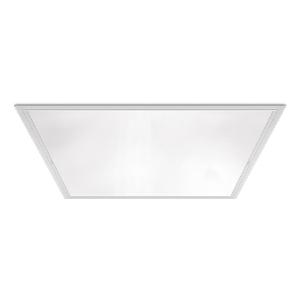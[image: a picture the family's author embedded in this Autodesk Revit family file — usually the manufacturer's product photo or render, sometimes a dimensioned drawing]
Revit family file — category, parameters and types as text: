
# Revit family: 3f_filippi_-_l_340_luce_diffusa_lgs_ip65v_3f_filippi_-_23977_-_l_340_45w-840_lgs_ip65v_621x621
name_source: partatom
category: Lighting Fixtures
units: mm (PartAtom-declared; Revit-internal decimal feet)

## family parameters
Cut with Voids When Loaded = No
Host = Face
Light Source = No
Part Type = Normal
Room Calculation Point = No
Round Connector Dimension = Use Diameter
Shared = No

## types (1)
- 3F Filippi - L 340 Luce Diffusa LGS IP65V (1 x LED, 6537 lm, 52 W, 4000 K)
    Apparent Load = 52 VA
    Approval mark = ENEC
    CIE Flux Codes = 67 92 98 100 100
    Color Rendering = 80
    Color Temperature = 4000 K
    Control Gear = Electronic ballast
    Default Elevation = 1800 mm
    Description = ILLUMINOTECHNICAL
Luminous efficiency 100% (DLOR 100%, ULOR 0%).
Initial luminous flux of the luminaire 6537 lm.
Direct symmetric distribution.
Installation Interdistance Transv.D = 1.19 x hu - Long.D = 1.17 x hu.
Average luminance <3000 cd/m² for radial angles >65°.
Tabular UGR (CIE 117 - 4H-8H; S=0.25H; 70/50/20): RUG 18.3 - 18.3.
Beam angle: 87° - 86°.
Luminous efficacy 126 lm/W.
Lifetime (L93/B10): 30000 h. (tq+25°C)
Lifetime (L90/B10): 50000 h. (tq+25°C)
Lifetime (L85/B10): 80000 h. (tq+25°C)
Lifetime (L80/B10): 100000 h. (tq+25°C)
Sudden decreased luminous flux after 50000 hours: 0% (C0).
Photobiological safety in compliance with IEC/TR 62778: RG0 risk exempt, (IEC 62471).
In compliance with IEC/EN 62722-2-1 - IEC/EN 62717 standards.

SOURCE
Squared LED module 45W/840.
Energy efficiency class (UE 2019/2020 - UE 2019/2015): C.
CIE 13.3 Colour rendering index: CRI >80 (R9 <50%).
IES TM-30 Fidelity Index: Rf = 84 Rg = 95.
CCT nominal colour temperature 4000 K.
Colour initial tolerance (MacAdam): SDCM 3.

MECHANICAL
Housing in hot-galvanised steel, painted in white polyester.
Perimetral frame in white polycarbonate.
LGS micro-prismatic flat diffuser in transparent methacrylate (PMMA), multi-lenticular exterior, anti-glare.
Anti-glare opal polycarbonate filter for brightness uniformity.
Luminaire with limited surface temperature. - D - (EN 60598-2-24)
Dimensions: 621x621 mm, height 80 mm. Weight 4.965 kg.
IP65 protection degree for exposed part, IP40 for recessed part.
Mechanical strength to impacts IK06 (1 joule).
Glow-wire test resistance 650°C.

ELECTRICAL
Wiring on a separate unit.
Halogen Free electronic wiring 230V-50/60Hz, power factor 0.95, THD <25%, constant output current, SELV, class II, 1 driver.
Power of the luminaire 52 W.
CE - IEC 60598-1 - EN 60598-1.
SAFE FLICKER: PstLM=<1 and SVM=<0.4 (IEC TR 61547-1 and IEC TR 63158), to ensure a more comfortable and safe light.
Luminaire compliant with EN 60598-2-22 for power supply from a centralised emergency system CPSS (Central Power Supply System), not incorporated in the luminaire - high risk areas excluded. The default power and flux are 100% in AC and 100% in DC.
Ambient temperature from 0°C to +40°C.
Temperature class T6 max 85°C.
Relative humidity UR: <85%.

INSTALLATION
Lay-in recessed fitting.
All accessories dedicated to this product are available on the Catalog and on our website www.3F-Filippi.com.

APPLICATIONS
Suitable product for food production plants (HACCP), IFS (Food Version 6), BRC (GSFS Food Version 7).
In environments requiring protection and simplified cleaning.
Hospitals, pharmaceutical, chemical, aseptic laboratories, sterilised rooms.
Environments: with VDTs, meeting rooms, offices.
Environments: architectural, commercial, staterooms, banks.
Environments where demanding visual tasks are performed and soft diffuse light is required for optimal visual comfort and total shielding of the light source.

WARNING
Luminaire designed for disposal/recycling at end-of-life.
Replaceable (LED only) light source by a professional. Replaceable control gear by a professional.
    Height = 0 mm  [stored 0 ft]
    Lamp = 1 x LED
    Lamp Light Flux = 6537 lm
    Lamp Power = 52 W
    Lamp count = 1
    Length = 621 mm
    Lifetime = 50000 h
    Luminous efficacy = 126 lm/W
    Manufacturer = 3F Filippi
    ModVariant = No
    Model = 3F Filippi - 23977 - L 340 45W-840 LGS IP65V 621x621
    Mounting Place = Ceiling
    Mounting Type = Recessed
    Number of Poles = 1
    OnlyDefault = Yes
    Power Factor = 1
    Product Name = 3F Filippi - L 340 Luce Diffusa LGS IP65V
    Product group = recessed luminaire
    ProductGroupID = 4
    Protection Class = Protection class II
    Protection Degree = IP 40
    RLX_Detail_Level = 1
    RLX_Emergency_Light_Flux = 0 lm
    RLX_Emergency_Type = 0
    RLX_Emergency_Type_DB = No
    RlxData = <blob elided: 160497 chars, md5=dcfd25d7>
    Socket = socket
    Standby Power = 0 W
    System Light Flux = 6537 lm
    System Power = 52 W
    Type Comments = Product without accessories
    Type Image = 3ffilippi_l_340_luce_diffusa_lgs_ip65v.jpg
    URL = http://relux.com
    VarID = ---
    Voltage = 0 V
    Weight = 0.00 kg
    Width = 621 mm

note: [stored X ft] marks values corroborated as IEEE doubles in the binary element streams (Revit-internal decimal feet)

## geometry (parser evidence)
native form markers: Blend x4, Sweep x11
no freeform markers — native parametric forms only
